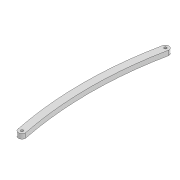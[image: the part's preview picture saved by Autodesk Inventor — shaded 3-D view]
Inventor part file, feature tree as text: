
AUTODESK INVENTOR PART (.ipt)
format: ipt  version: 2022 (Build 260153000, 153)  size: 93,184 bytes
history: native  units: mm
features: extrude x1, sketch x1
ambient origin geometry x8: Origin, YZ Plane, XZ Plane, XY Plane, X Axis, Y Axis, Z Axis, Center Point
bodies: Solid1 (feature_tree)
feature tree (2):
  extrude  "Extrusion1"  Depth=300.0mm
  sketch  "Sketch1"  dims[d0=2.2mm d1=2.2mm d2=6.0mm d3=120.239mm d6=4.0mm d7=0.0mm d14=300.0mm d15=300.0mm]
